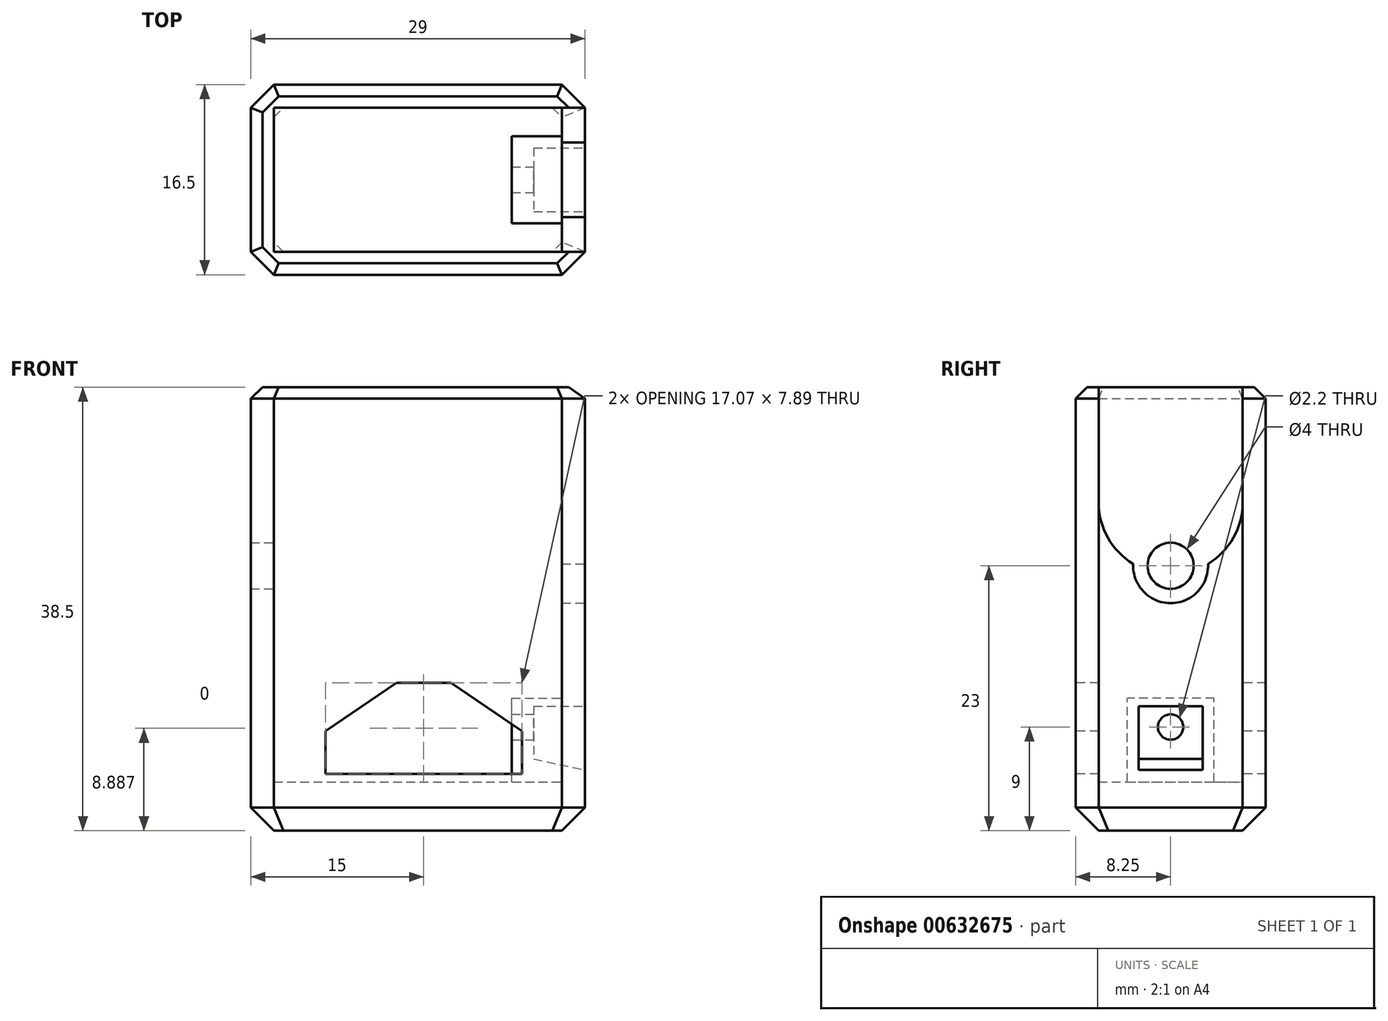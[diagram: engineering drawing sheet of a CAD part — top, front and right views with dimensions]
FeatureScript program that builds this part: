
annotation { "Feature Type Name" : "Feature", "Feature Type Description" : "" }
export const myFeature = defineFeature(function(context is Context, id is Id, definition is map)
    precondition{}
    {
        {
            var Q0;
            Q0=qCreatedBy(makeId("Top.planeOp"),FACE);
            var sketch = newSketch(context, id + "F0", { "sketchPlane" : qUnion([Q0])});
            skLineSegment(sketch, "E0.bottom", {"start": v(0, 0) * mm, "end": v(29, 0) * mm});
            skLineSegment(sketch, "E0.top", {"start": v(0, 16.5) * mm, "end": v(29, 16.5) * mm});
            skLineSegment(sketch, "E0.left", {"start": v(0, 0) * mm, "end": v(0, 16.5) * mm});
            skLineSegment(sketch, "E0.right", {"start": v(29, 0) * mm, "end": v(29, 16.5) * mm});
            skSolve(sketch);
        }
        {
            var Q0;
            Q0 = qSketchRegion(id + "F0", true);
            extrude(context, id + "F1", {"entities" : qUnion([Q0]), "depth" : 38.5 * mm, "offsetDistance" : 25 * mm});
        }
        {
            var Q0;
            Q0=makeQuery(id+"F1.opExtrude","CAP_FACE",FACE,{"disambiguationData":[OSD([sQuery(id+"F0.wireOp",EDGE,"E0.bottom"),sQuery(id+"F0.wireOp",EDGE,"E0.top"),sQuery(id+"F0.wireOp",EDGE,"E0.left"),sQuery(id+"F0.wireOp",EDGE,"E0.right")])],"isStart":false});
            shell(context, id + "F2", {"entities" : qUnion([Q0]), "thickness" : 2 * mm});
        }
        {
            var Q0;
            Q0=makeQuery(id+"F2.opShell","OFFSET_FACE",FACE,{"disambiguationData":[OSD([sQuery(id+"F0.wireOp",EDGE,"E0.bottom"),sQuery(id+"F0.wireOp",EDGE,"E0.top"),sQuery(id+"F0.wireOp",EDGE,"E0.left"),sQuery(id+"F0.wireOp",EDGE,"E0.right")])]});
            extrude(context, id + "F3", {"entities" : qUnion([Q0]), "operationType" : NewBodyOperationType.ADD, "depth" : 2.25 * mm, "offsetDistance" : 25 * mm});
        }
        {
            var Q0;
            Q0=makeQuery(id+"F1.opExtrude","SWEPT_EDGE",EDGE,{"disambiguationData":[OSD([sQuery(id+"F0.wireOp",EDGE,"E0.bottom"),sQuery(id+"F0.wireOp",EDGE,"E0.right")])]});
            var Q1;
            Q1=makeQuery(id+"F1.opExtrude","SWEPT_EDGE",EDGE,{"disambiguationData":[OSD([sQuery(id+"F0.wireOp",EDGE,"E0.bottom"),sQuery(id+"F0.wireOp",EDGE,"E0.left")])]});
            var Q2;
            Q2=makeQuery(id+"F1.opExtrude","SWEPT_EDGE",EDGE,{"disambiguationData":[OSD([sQuery(id+"F0.wireOp",EDGE,"E0.top"),sQuery(id+"F0.wireOp",EDGE,"E0.right")])]});
            var Q3;
            Q3=makeQuery(id+"F1.opExtrude","SWEPT_EDGE",EDGE,{"disambiguationData":[OSD([sQuery(id+"F0.wireOp",EDGE,"E0.top"),sQuery(id+"F0.wireOp",EDGE,"E0.left")])]});
            chamfer(context, id + "F4", {"entities" : qUnion([Q0, Q1, Q2, Q3]), "width" : 2 * mm, "tangentPropagation" : true});
        }
        {
            var Q0;
            Q0=makeQuery(id+"F1.opExtrude","CAP_FACE",FACE,{"disambiguationData":[OSD([sQuery(id+"F0.wireOp",EDGE,"E0.bottom"),sQuery(id+"F0.wireOp",EDGE,"E0.top"),sQuery(id+"F0.wireOp",EDGE,"E0.left"),sQuery(id+"F0.wireOp",EDGE,"E0.right")])],"isStart":true});
            chamfer(context, id + "F5", {"entities" : qUnion([Q0]), "width" : 2 * mm, "tangentPropagation" : true});
        }
        {
            var Q0;
            Q0=makeQuery(id+"F1.opExtrude","CAP_EDGE",EDGE,{"disambiguationData":[OSD([sQuery(id+"F0.wireOp",EDGE,"E0.bottom")])],"isStart":false});
            var Q1;
            {var subQ0=sQuery(id+"F0.wireOp",EDGE,"E0.left");var subQ1=sQuery(id+"F0.wireOp",EDGE,"E0.bottom");Q1=makeQuery(id+"F4.opChamfer","BLEND_EDGE",EDGE,{"blendedFrom":[makeQuery(id+"F1.opExtrude","SWEPT_EDGE",EDGE,{"disambiguationData":[OSD([subQ1,subQ0])]}),makeQuery(id+"F1.opExtrude","CAP_FACE",FACE,{"disambiguationData":[OSD([subQ1,sQuery(id+"F0.wireOp",EDGE,"E0.top"),subQ0,sQuery(id+"F0.wireOp",EDGE,"E0.right")])],"isStart":false})],"blendedInto":[makeQuery(id+"F1.opExtrude","CAP_FACE",FACE,{"disambiguationData":[OSD([subQ1,sQuery(id+"F0.wireOp",EDGE,"E0.top"),subQ0,sQuery(id+"F0.wireOp",EDGE,"E0.right")])],"isStart":false})]});}
            var Q2;
            Q2=makeQuery(id+"F1.opExtrude","CAP_EDGE",EDGE,{"disambiguationData":[OSD([sQuery(id+"F0.wireOp",EDGE,"E0.left")])],"isStart":false});
            var Q3;
            {var subQ0=sQuery(id+"F0.wireOp",EDGE,"E0.left");var subQ1=sQuery(id+"F0.wireOp",EDGE,"E0.top");Q3=makeQuery(id+"F4.opChamfer","BLEND_EDGE",EDGE,{"blendedFrom":[makeQuery(id+"F1.opExtrude","SWEPT_EDGE",EDGE,{"disambiguationData":[OSD([subQ1,subQ0])]}),makeQuery(id+"F1.opExtrude","CAP_FACE",FACE,{"disambiguationData":[OSD([sQuery(id+"F0.wireOp",EDGE,"E0.bottom"),subQ1,subQ0,sQuery(id+"F0.wireOp",EDGE,"E0.right")])],"isStart":false})],"blendedInto":[makeQuery(id+"F1.opExtrude","CAP_FACE",FACE,{"disambiguationData":[OSD([sQuery(id+"F0.wireOp",EDGE,"E0.bottom"),subQ1,subQ0,sQuery(id+"F0.wireOp",EDGE,"E0.right")])],"isStart":false})]});}
            var Q4;
            Q4=makeQuery(id+"F1.opExtrude","CAP_EDGE",EDGE,{"disambiguationData":[OSD([sQuery(id+"F0.wireOp",EDGE,"E0.top")])],"isStart":false});
            var Q5;
            {var subQ0=sQuery(id+"F0.wireOp",EDGE,"E0.right");var subQ1=sQuery(id+"F0.wireOp",EDGE,"E0.top");Q5=makeQuery(id+"F4.opChamfer","BLEND_EDGE",EDGE,{"blendedFrom":[makeQuery(id+"F1.opExtrude","SWEPT_EDGE",EDGE,{"disambiguationData":[OSD([subQ1,subQ0])]}),makeQuery(id+"F1.opExtrude","CAP_FACE",FACE,{"disambiguationData":[OSD([sQuery(id+"F0.wireOp",EDGE,"E0.bottom"),subQ1,sQuery(id+"F0.wireOp",EDGE,"E0.left"),subQ0])],"isStart":false})],"blendedInto":[makeQuery(id+"F1.opExtrude","CAP_FACE",FACE,{"disambiguationData":[OSD([sQuery(id+"F0.wireOp",EDGE,"E0.bottom"),subQ1,sQuery(id+"F0.wireOp",EDGE,"E0.left"),subQ0])],"isStart":false})]});}
            var Q6;
            Q6=makeQuery(id+"F1.opExtrude","CAP_EDGE",EDGE,{"disambiguationData":[OSD([sQuery(id+"F0.wireOp",EDGE,"E0.right")])],"isStart":false});
            var Q7;
            {var subQ0=sQuery(id+"F0.wireOp",EDGE,"E0.right");var subQ1=sQuery(id+"F0.wireOp",EDGE,"E0.bottom");Q7=makeQuery(id+"F4.opChamfer","BLEND_EDGE",EDGE,{"blendedFrom":[makeQuery(id+"F1.opExtrude","SWEPT_EDGE",EDGE,{"disambiguationData":[OSD([subQ1,subQ0])]}),makeQuery(id+"F1.opExtrude","CAP_FACE",FACE,{"disambiguationData":[OSD([subQ1,sQuery(id+"F0.wireOp",EDGE,"E0.top"),sQuery(id+"F0.wireOp",EDGE,"E0.left"),subQ0])],"isStart":false})],"blendedInto":[makeQuery(id+"F1.opExtrude","CAP_FACE",FACE,{"disambiguationData":[OSD([subQ1,sQuery(id+"F0.wireOp",EDGE,"E0.top"),sQuery(id+"F0.wireOp",EDGE,"E0.left"),subQ0])],"isStart":false})]});}
            chamfer(context, id + "F6", {"entities" : qUnion([Q0, Q1, Q2, Q3, Q4, Q5, Q6, Q7]), "width" : 1 * mm, "tangentPropagation" : true});
        }
        {
            var Q0;
            Q0=makeQuery(id+"F1.opExtrude","SWEPT_FACE",FACE,{"disambiguationData":[OSD([sQuery(id+"F0.wireOp",EDGE,"E0.bottom")])]});
            var sketch = newSketch(context, id + "F7", { "sketchPlane" : qUnion([Q0])});
            skLineSegment(sketch, "E1", {"start": v(6.46, 4.94) * mm, "end": v(23.54, 4.94) * mm});
            skLineSegment(sketch, "E2", {"start": v(23.54, 4.94) * mm, "end": v(23.54, 8.66) * mm});
            skLineSegment(sketch, "E3", {"start": v(23.54, 8.66) * mm, "end": v(17.36, 12.83) * mm});
            skLineSegment(sketch, "E4", {"start": v(17.36, 12.83) * mm, "end": v(12.63, 12.83) * mm});
            skLineSegment(sketch, "E5", {"start": v(12.63, 12.83) * mm, "end": v(6.46, 8.66) * mm});
            skLineSegment(sketch, "E6", {"start": v(6.46, 8.66) * mm, "end": v(6.46, 4.94) * mm});
            skSolve(sketch);
        }
        {
            var Q0;
            Q0=makeQuery(id+"F7.imprint","IMPRINT",FACE,{"disambiguationData":[TD([[makeQuery(id+"F7.imprint","IMPRINT",EDGE,{"derivedFrom":sQuery(id+"F7.wireOp",EDGE,"E1")}),1.0]])]});
            extrude(context, id + "F8", {"entities" : qUnion([Q0]), "operationType" : NewBodyOperationType.REMOVE, "endBound" : BoundingType.THROUGH_ALL, "oppositeDirection" : true, "depth" : 25 * mm, "offsetDistance" : 25 * mm});
        }
        {
            var Q0;
            Q0=makeQuery(id+"F1.opExtrude","SWEPT_FACE",FACE,{"disambiguationData":[OSD([sQuery(id+"F0.wireOp",EDGE,"E0.right")])]});
            var sketch = newSketch(context, id + "F9", { "sketchPlane" : qUnion([Q0])});
            skCircle(sketch, "E7", {"center": v(8.25, 23) * mm, "radius": 3.25 * mm});
            skCircle(sketch, "E8", {"center": v(8.25, 28.5) * mm, "radius": 6.25 * mm});
            skLineSegment(sketch, "E9.bottom", {"start": v(2, 28.5) * mm, "end": v(14.5, 28.5) * mm});
            skLineSegment(sketch, "E9.top", {"start": v(2, 38.5) * mm, "end": v(14.5, 38.5) * mm});
            skLineSegment(sketch, "E9.left", {"start": v(2, 28.5) * mm, "end": v(2, 38.5) * mm});
            skLineSegment(sketch, "E9.right", {"start": v(14.5, 28.5) * mm, "end": v(14.5, 38.5) * mm});
            skSolve(sketch);
        }
        {
            var Q0;
            {var subQ0=sQuery(id+"F9.wireOp",EDGE,"E8");var subQ1=sQuery(id+"F9.wireOp",EDGE,"E7");var subQ2=makeQuery(id+"F9.imprint","INTERSECT",VERTEX,{"disambiguationData":[OD(0.0)],"derivedFrom":[subQ1,subQ0]});Q0=makeQuery(id+"F9.imprint","IMPRINT",FACE,{"disambiguationData":[TD([[makeQuery(id+"F9.imprint","IMPRINT",EDGE,{"disambiguationData":[TD([[subQ2,-1.0]])],"derivedFrom":subQ1}),1.0]])]});}
            var Q1;
            {var subQ0=sQuery(id+"F9.wireOp",EDGE,"E8");var subQ1=sQuery(id+"F9.wireOp",EDGE,"E7");var subQ2=makeQuery(id+"F9.imprint","INTERSECT",VERTEX,{"disambiguationData":[OD(0.0)],"derivedFrom":[subQ1,subQ0]});Q1=makeQuery(id+"F9.imprint","IMPRINT",FACE,{"disambiguationData":[TD([[makeQuery(id+"F9.imprint","IMPRINT",EDGE,{"disambiguationData":[TD([[subQ2,1.0]])],"derivedFrom":subQ1}),1.0]])]});}
            var Q2;
            {var subQ4=sQuery(id+"F9.wireOp",EDGE,"E9.bottom");Q2=makeQuery(id+"F9.imprint","IMPRINT",FACE,{"disambiguationData":[TD([[makeQuery(id+"F9.imprint","IMPRINT",EDGE,{"derivedFrom":subQ4}),-1.0]])]});}
            var Q3;
            {var subQ0=sQuery(id+"F9.wireOp",EDGE,"E9.bottom");Q3=makeQuery(id+"F9.imprint","IMPRINT",FACE,{"disambiguationData":[TD([[makeQuery(id+"F9.imprint","IMPRINT",EDGE,{"derivedFrom":subQ0}),1.0]])]});}
            var Q4;
            {var subQ3=sQuery(id+"F0.wireOp",EDGE,"E0.right");var subQ4=makeQuery(id+"F1.opExtrude","SWEPT_FACE",FACE,{"disambiguationData":[OSD([subQ3])]});var subQ8=makeQuery(id+"F6.opChamfer","BLEND_EDGE",EDGE,{"blendedFrom":[makeQuery(id+"F1.opExtrude","CAP_EDGE",EDGE,{"disambiguationData":[OSD([subQ3])],"isStart":false}),subQ4],"blendedInto":[subQ4]});Q4=makeQuery(id+"F9.imprint","IMPRINT",FACE,{"disambiguationData":[TD([[makeQuery(id+"F9.imprint","IMPRINT",EDGE,{"derivedFrom":subQ8}),1.0]])]});}
            var Q5;
            {var subQ0=sQuery(id+"F9.wireOp",EDGE,"E9.top");Q5=makeQuery(id+"F9.imprint","IMPRINT",FACE,{"disambiguationData":[TD([[makeQuery(id+"F9.imprint","IMPRINT",EDGE,{"derivedFrom":subQ0}),-1.0]])]});}
            extrude(context, id + "F10", {"entities" : qUnion([Q0, Q1, Q2, Q3, Q4, Q5]), "operationType" : NewBodyOperationType.REMOVE, "endBound" : BoundingType.UP_TO_NEXT, "oppositeDirection" : true, "depth" : 25 * mm, "offsetDistance" : 25 * mm});
        }
        {
            var Q0;
            Q0=makeQuery(id+"F2.opShell","OFFSET_FACE",FACE,{"disambiguationData":[OSD([sQuery(id+"F0.wireOp",EDGE,"E0.left")])]});
            var sketch = newSketch(context, id + "F11", { "sketchPlane" : qUnion([Q0])});
            skCircle(sketch, "E10", {"center": v(8.25, 23) * mm, "radius": 2 * mm});
            skSolve(sketch);
        }
        {
            var Q0;
            Q0=makeQuery(id+"F11.imprint","IMPRINT",FACE,{"disambiguationData":[TD([[makeQuery(id+"F11.imprint","IMPRINT",EDGE,{"derivedFrom":sQuery(id+"F11.wireOp",EDGE,"E10")}),1.0]])]});
            extrude(context, id + "F12", {"entities" : qUnion([Q0]), "operationType" : NewBodyOperationType.REMOVE, "endBound" : BoundingType.THROUGH_ALL, "oppositeDirection" : true, "depth" : 25 * mm, "offsetDistance" : 25 * mm});
        }
        {
            var Q0;
            Q0=makeQuery(id+"F2.opShell","OFFSET_FACE",FACE,{"disambiguationData":[OSD([sQuery(id+"F0.wireOp",EDGE,"E0.right")])]});
            var sketch = newSketch(context, id + "F13", { "sketchPlane" : qUnion([Q0])});
            skLineSegment(sketch, "E11.bottom", {"start": v(-12.02, 4.25) * mm, "end": v(-4.48, 4.25) * mm});
            skLineSegment(sketch, "E11.top", {"start": v(-12.02, 11.5) * mm, "end": v(-4.48, 11.5) * mm});
            skLineSegment(sketch, "E11.left", {"start": v(-12.02, 4.25) * mm, "end": v(-12.02, 11.5) * mm});
            skLineSegment(sketch, "E11.right", {"start": v(-4.48, 4.25) * mm, "end": v(-4.48, 11.5) * mm});
            skCircle(sketch, "E12", {"center": v(-8.25, 9) * mm, "radius": 1.1 * mm});
            skSolve(sketch);
        }
        {
            var Q0;
            Q0 = qSketchRegion(id + "F13", true);
            extrude(context, id + "F14", {"entities" : qUnion([Q0]), "operationType" : NewBodyOperationType.ADD, "depth" : 4.35 * mm, "offsetDistance" : 25 * mm});
        }
        {
            var Q0;
            Q0=makeQuery(id+"F1.opExtrude","SWEPT_FACE",FACE,{"disambiguationData":[OSD([sQuery(id+"F0.wireOp",EDGE,"E0.right")])]});
            var sketch = newSketch(context, id + "F15", { "sketchPlane" : qUnion([Q0])});
            skLineSegment(sketch, "E13.bottom", {"start": v(5.48, 5.27) * mm, "end": v(11.02, 5.27) * mm});
            skLineSegment(sketch, "E13.top", {"start": v(5.48, 10.8) * mm, "end": v(11.02, 10.8) * mm});
            skLineSegment(sketch, "E13.left", {"start": v(5.48, 5.27) * mm, "end": v(5.48, 10.8) * mm});
            skLineSegment(sketch, "E13.right", {"start": v(11.02, 5.27) * mm, "end": v(11.02, 10.8) * mm});
            skSolve(sketch);
        }
        {
            var Q0;
            Q0=makeQuery(id+"F15.imprint","IMPRINT",FACE,{"disambiguationData":[TD([[makeQuery(id+"F15.imprint","IMPRINT",EDGE,{"derivedFrom":sQuery(id+"F15.wireOp",EDGE,"E13.bottom")}),-1.0]])]});
            cPlane(context, id + "F16", {"entities" : qUnion([Q0]), "cplaneType" : CPlaneType.OFFSET, "offset" : 4.45 * mm, "oppositeDirection" : true, "width" : 150 * mm, "height" : 150 * mm});
        }
        {
            var Q0;
            Q0=qCreatedBy(id+"F16.planeOp",FACE);
            var sketch = newSketch(context, id + "F17", { "sketchPlane" : qUnion([Q0])});
            skLineSegment(sketch, "E14.bottom", {"start": v(11.02, 10.8) * mm, "end": v(5.48, 10.8) * mm});
            skLineSegment(sketch, "E14.top", {"start": v(11.02, 6.22) * mm, "end": v(5.48, 6.22) * mm});
            skLineSegment(sketch, "E14.left", {"start": v(11.02, 10.8) * mm, "end": v(11.02, 6.22) * mm});
            skLineSegment(sketch, "E14.right", {"start": v(5.48, 10.8) * mm, "end": v(5.48, 6.22) * mm});
            skSolve(sketch);
        }
        {
            var Q1;
            Q1 = qSketchRegion(id + "F17", true);
            var Q2;
            Q2 = qSketchRegion(id + "F15", true);
            loft(context, id + "F18", {"operationType" : NewBodyOperationType.REMOVE, "sheetProfilesArray" : [{ "sheetProfileEntities" : qUnion([Q1]) }, { "sheetProfileEntities" : qUnion([Q2]) }]});
        }
    });
